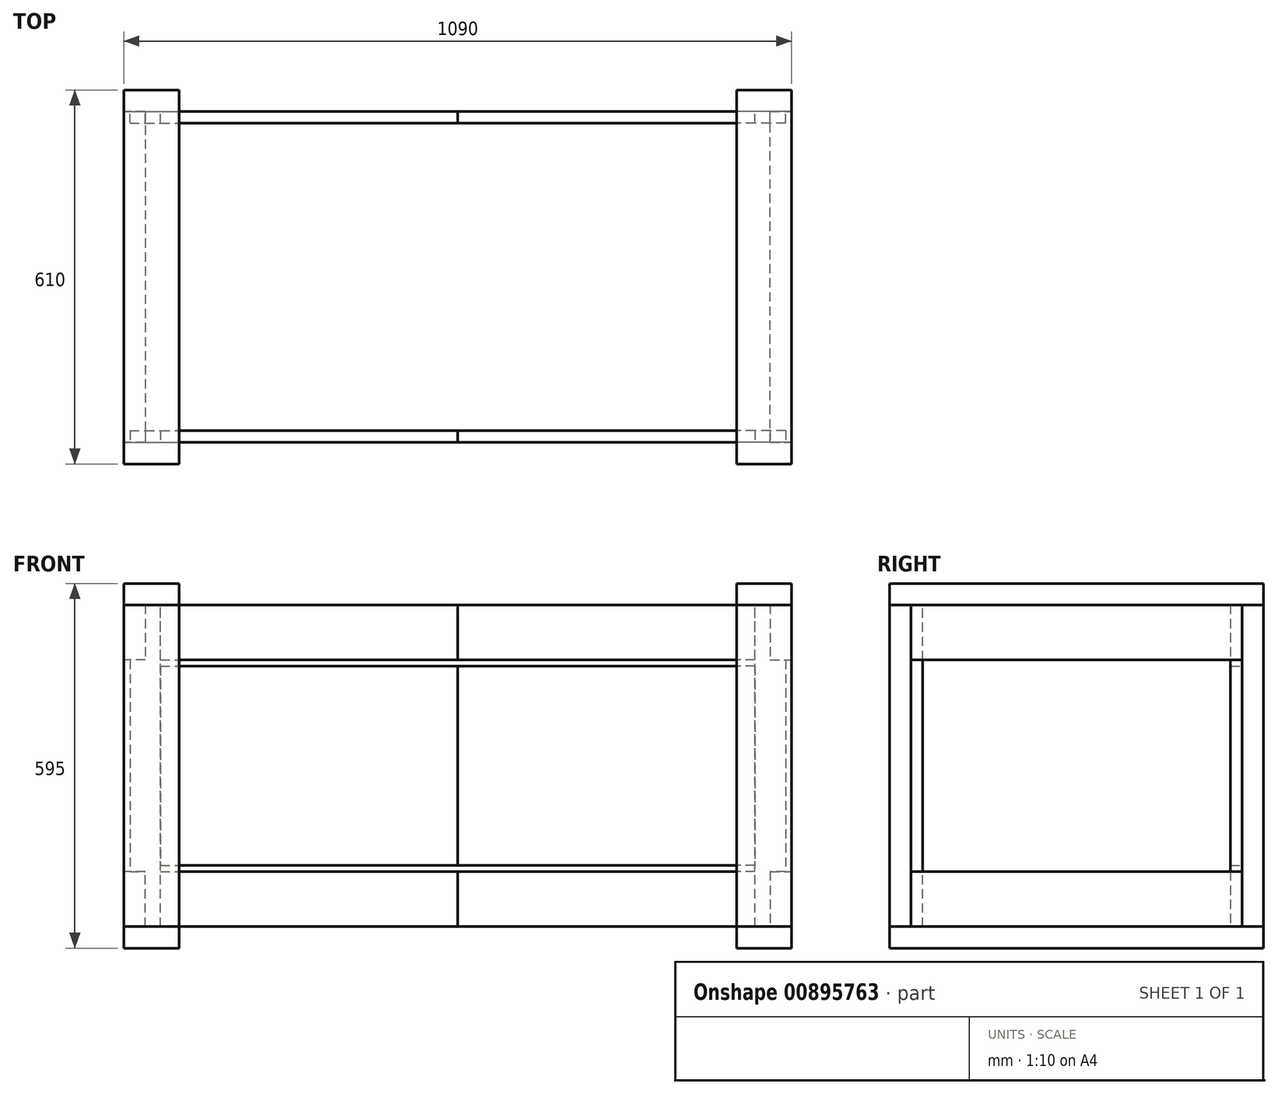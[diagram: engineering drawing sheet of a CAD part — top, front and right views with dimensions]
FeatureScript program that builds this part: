
annotation { "Feature Type Name" : "Feature", "Feature Type Description" : "" }
export const myFeature = defineFeature(function(context is Context, id is Id, definition is map)
    precondition{}
    {
        {
            var Q0;
            Q0=qCreatedBy(makeId("Top.planeOp"),FACE);
            var sketch = newSketch(context, id + "F0", { "sketchPlane" : qUnion([Q0])});
            skLineSegment(sketch, "E0.bottom", {"start": v(-545, 305) * mm, "end": v(-455, 305) * mm});
            skLineSegment(sketch, "E0.top", {"start": v(-545, -305) * mm, "end": v(-455, -305) * mm});
            skLineSegment(sketch, "E0.left", {"start": v(-545, 305) * mm, "end": v(-545, -305) * mm});
            skLineSegment(sketch, "E0.right", {"start": v(-455, 305) * mm, "end": v(-455, -305) * mm});
            skLineSegment(sketch, "E1.bottom", {"start": v(455, 305) * mm, "end": v(545, 305) * mm});
            skLineSegment(sketch, "E1.top", {"start": v(455, -305) * mm, "end": v(545, -305) * mm});
            skLineSegment(sketch, "E1.left", {"start": v(455, 305) * mm, "end": v(455, -305) * mm});
            skLineSegment(sketch, "E1.right", {"start": v(545, 305) * mm, "end": v(545, -305) * mm});
            skLineSegment(sketch, "E2", {"start": v(-455, 0) * mm, "end": v(455, 0) * mm, "construction": true});
            skSolve(sketch);
        }
        {
            var Q0;
            Q0 = qSketchRegion(id + "F0", true);
            extrude(context, id + "F1", {"entities" : qUnion([Q0]), "depth" : 35 * mm, "offsetDistance" : 25 * mm});
        }
        {
            var Q0;
            Q0=makeQuery(id+"F1.opExtrude","CAP_FACE",FACE,{"disambiguationData":[OSD([sQuery(id+"F0.wireOp",EDGE,"E0.bottom"),sQuery(id+"F0.wireOp",EDGE,"E0.top"),sQuery(id+"F0.wireOp",EDGE,"E0.left"),sQuery(id+"F0.wireOp",EDGE,"E0.right")])],"isStart":false});
            var sketch = newSketch(context, id + "F2", { "sketchPlane" : qUnion([Q0])});
            skLineSegment(sketch, "E3.bottom", {"start": v(-545, 305) * mm, "end": v(-455, 305) * mm});
            skLineSegment(sketch, "E3.top", {"start": v(-545, 270) * mm, "end": v(-455, 270) * mm});
            skLineSegment(sketch, "E3.left", {"start": v(-545, 305) * mm, "end": v(-545, 270) * mm});
            skLineSegment(sketch, "E3.right", {"start": v(-455, 305) * mm, "end": v(-455, 270) * mm});
            skLineSegment(sketch, "E4.bottom", {"start": v(-545, -305) * mm, "end": v(-455, -305) * mm});
            skLineSegment(sketch, "E4.top", {"start": v(-545, -270) * mm, "end": v(-455, -270) * mm});
            skLineSegment(sketch, "E4.left", {"start": v(-545, -305) * mm, "end": v(-545, -270) * mm});
            skLineSegment(sketch, "E4.right", {"start": v(-455, -305) * mm, "end": v(-455, -270) * mm});
            skLineSegment(sketch, "E5.bottom", {"start": v(545, 305) * mm, "end": v(455, 305) * mm});
            skLineSegment(sketch, "E5.top", {"start": v(545, 270) * mm, "end": v(455, 270) * mm});
            skLineSegment(sketch, "E5.left", {"start": v(545, 305) * mm, "end": v(545, 270) * mm});
            skLineSegment(sketch, "E5.right", {"start": v(455, 305) * mm, "end": v(455, 270) * mm});
            skLineSegment(sketch, "E6.bottom", {"start": v(545, -305) * mm, "end": v(455, -305) * mm});
            skLineSegment(sketch, "E6.top", {"start": v(545, -270) * mm, "end": v(455, -270) * mm});
            skLineSegment(sketch, "E6.left", {"start": v(545, -305) * mm, "end": v(545, -270) * mm});
            skLineSegment(sketch, "E6.right", {"start": v(455, -305) * mm, "end": v(455, -270) * mm});
            skSolve(sketch);
        }
        {
            var Q0;
            Q0 = qSketchRegion(id + "F2", true);
            extrude(context, id + "F3", {"entities" : qUnion([Q0]), "depth" : 525 * mm, "offsetDistance" : 25 * mm});
        }
        {
            var Q0;
            Q0=makeQuery(id+"F3.opExtrude","CAP_FACE",FACE,{"disambiguationData":[OSD([sQuery(id+"F2.wireOp",EDGE,"E3.bottom"),sQuery(id+"F2.wireOp",EDGE,"E3.top"),sQuery(id+"F2.wireOp",EDGE,"E3.left"),sQuery(id+"F2.wireOp",EDGE,"E3.right")])],"isStart":false});
            var sketch = newSketch(context, id + "F4", { "sketchPlane" : qUnion([Q0])});
            skLineSegment(sketch, "E7.0.0", {"start": v(-545, 305) * mm, "end": v(-545, -305) * mm});
            skLineSegment(sketch, "E7.0.1", {"start": v(-545, -305) * mm, "end": v(-455, -305) * mm});
            skLineSegment(sketch, "E7.0.2", {"start": v(-455, -305) * mm, "end": v(-455, 305) * mm});
            skLineSegment(sketch, "E7.0.3", {"start": v(-455, 305) * mm, "end": v(-545, 305) * mm});
            skLineSegment(sketch, "E7.1.0", {"start": v(455, 305) * mm, "end": v(455, -305) * mm});
            skLineSegment(sketch, "E7.1.1", {"start": v(455, -305) * mm, "end": v(545, -305) * mm});
            skLineSegment(sketch, "E7.1.2", {"start": v(545, -305) * mm, "end": v(545, 305) * mm});
            skLineSegment(sketch, "E7.1.3", {"start": v(545, 305) * mm, "end": v(455, 305) * mm});
            skSolve(sketch);
        }
        {
            var Q0;
            Q0 = qSketchRegion(id + "F4", true);
            extrude(context, id + "F5", {"entities" : qUnion([Q0]), "depth" : 35 * mm, "offsetDistance" : 25 * mm});
        }
        {
            var Q0;
            Q0=makeQuery(id+"F1.opExtrude","SWEPT_FACE",FACE,{"disambiguationData":[OSD([sQuery(id+"F0.wireOp",EDGE,"E1.right")])]});
            var sketch = newSketch(context, id + "F6", { "sketchPlane" : qUnion([Q0])});
            skLineSegment(sketch, "E8.bottom", {"start": v(-270, 35) * mm, "end": v(270, 35) * mm});
            skLineSegment(sketch, "E8.top", {"start": v(-270, 125) * mm, "end": v(270, 125) * mm});
            skLineSegment(sketch, "E8.left", {"start": v(-270, 35) * mm, "end": v(-270, 125) * mm});
            skLineSegment(sketch, "E8.right", {"start": v(270, 35) * mm, "end": v(270, 125) * mm});
            skLineSegment(sketch, "E9.bottom", {"start": v(-270, 560) * mm, "end": v(270, 560) * mm});
            skLineSegment(sketch, "E9.top", {"start": v(-270, 470) * mm, "end": v(270, 470) * mm});
            skLineSegment(sketch, "E9.left", {"start": v(-270, 560) * mm, "end": v(-270, 470) * mm});
            skLineSegment(sketch, "E9.right", {"start": v(270, 560) * mm, "end": v(270, 470) * mm});
            skSolve(sketch);
        }
        {
            var Q0;
            Q0 = qSketchRegion(id + "F6", true);
            extrude(context, id + "F7", {"entities" : qUnion([Q0]), "oppositeDirection" : true, "depth" : 35 * mm, "offsetDistance" : 25 * mm});
        }
        {
            var Q0;
            Q0=makeQuery(id+"F3.opExtrude","SWEPT_FACE",FACE,{"disambiguationData":[OSD([sQuery(id+"F2.wireOp",EDGE,"E5.top")])]});
            var sketch = newSketch(context, id + "F8", { "sketchPlane" : qUnion([Q0])});
            skLineSegment(sketch, "E10", {"start": v(485, 35) * mm, "end": v(485, 560) * mm});
            skLineSegment(sketch, "E11", {"start": v(485, 560) * mm, "end": v(510, 560) * mm});
            skLineSegment(sketch, "E12", {"start": v(510, 560) * mm, "end": v(510, 470) * mm});
            skLineSegment(sketch, "E13", {"start": v(510, 470) * mm, "end": v(535, 470) * mm});
            skLineSegment(sketch, "E14", {"start": v(535, 470) * mm, "end": v(535, 125) * mm});
            skLineSegment(sketch, "E15", {"start": v(535, 125) * mm, "end": v(510, 125) * mm});
            skLineSegment(sketch, "E16", {"start": v(510, 125) * mm, "end": v(510, 35) * mm});
            skLineSegment(sketch, "E17", {"start": v(510, 35) * mm, "end": v(485, 35) * mm});
            skSolve(sketch);
        }
        {
            var Q0;
            Q0 = qSketchRegion(id + "F8", true);
            extrude(context, id + "F9", {"entities" : qUnion([Q0]), "depth" : 19 * mm, "offsetDistance" : 25 * mm});
        }
        {
            var Q0;
            Q0=makeQuery(id+"F9.opExtrude","SWEPT_BODY",BODY,{"disambiguationData":[OSD([sQuery(id+"F8.wireOp",EDGE,"E10"),sQuery(id+"F8.wireOp",EDGE,"E11"),sQuery(id+"F8.wireOp",EDGE,"E12"),sQuery(id+"F8.wireOp",EDGE,"E13"),sQuery(id+"F8.wireOp",EDGE,"E14"),sQuery(id+"F8.wireOp",EDGE,"E15"),sQuery(id+"F8.wireOp",EDGE,"E16"),sQuery(id+"F8.wireOp",EDGE,"E17")])]});
            var Q1;
            Q1=qCreatedBy(makeId("Front.planeOp"),FACE);
            mirror(context, id + "F10", {"entities" : qUnion([Q0]), "mirrorPlane" : qUnion([Q1])});
        }
        {
            var Q0;
            Q0=makeQuery(id+"F3.opExtrude","SWEPT_FACE",FACE,{"disambiguationData":[OSD([sQuery(id+"F2.wireOp",EDGE,"E5.top")])]});
            var sketch = newSketch(context, id + "F11", { "sketchPlane" : qUnion([Q0])});
            skLineSegment(sketch, "E18.bottom", {"start": v(485, 460) * mm, "end": v(0, 460) * mm});
            skLineSegment(sketch, "E18.top", {"start": v(485, 135) * mm, "end": v(0, 135) * mm});
            skLineSegment(sketch, "E18.left", {"start": v(485, 460) * mm, "end": v(485, 135) * mm});
            skLineSegment(sketch, "E18.right", {"start": v(0, 460) * mm, "end": v(0, 135) * mm});
            skSolve(sketch);
        }
        {
            var Q0;
            Q0 = qSketchRegion(id + "F11", true);
            extrude(context, id + "F12", {"entities" : qUnion([Q0]), "depth" : 19 * mm, "offsetDistance" : 25 * mm});
        }
        {
            var Q0;
            Q0=makeQuery(id+"F3.opExtrude","SWEPT_FACE",FACE,{"disambiguationData":[OSD([sQuery(id+"F2.wireOp",EDGE,"E6.top")])]});
            var sketch = newSketch(context, id + "F13", { "sketchPlane" : qUnion([Q0])});
            skLineSegment(sketch, "E19.bottom", {"start": v(-485, 470) * mm, "end": v(0, 470) * mm});
            skLineSegment(sketch, "E19.top", {"start": v(-485, 560) * mm, "end": v(0, 560) * mm});
            skLineSegment(sketch, "E19.left", {"start": v(-485, 470) * mm, "end": v(-485, 560) * mm});
            skLineSegment(sketch, "E19.right", {"start": v(0, 470) * mm, "end": v(0, 560) * mm});
            skLineSegment(sketch, "E20.bottom", {"start": v(-485, 35) * mm, "end": v(0, 35) * mm});
            skLineSegment(sketch, "E20.top", {"start": v(-485, 125) * mm, "end": v(0, 125) * mm});
            skLineSegment(sketch, "E20.left", {"start": v(-485, 35) * mm, "end": v(-485, 125) * mm});
            skLineSegment(sketch, "E20.right", {"start": v(0, 35) * mm, "end": v(0, 125) * mm});
            skSolve(sketch);
        }
        {
            var Q0;
            Q0 = qSketchRegion(id + "F13", true);
            extrude(context, id + "F14", {"entities" : qUnion([Q0]), "depth" : 19 * mm, "offsetDistance" : 25 * mm});
        }
        {
            var Q0;
            Q0=makeQuery(id+"F7.opExtrude","SWEPT_BODY",BODY,{"disambiguationData":[OSD([sQuery(id+"F6.wireOp",EDGE,"E8.bottom"),sQuery(id+"F6.wireOp",EDGE,"E8.top"),sQuery(id+"F6.wireOp",EDGE,"E8.left"),sQuery(id+"F6.wireOp",EDGE,"E8.right")])]});
            var Q1;
            Q1=makeQuery(id+"F7.opExtrude","SWEPT_BODY",BODY,{"disambiguationData":[OSD([sQuery(id+"F6.wireOp",EDGE,"E9.bottom"),sQuery(id+"F6.wireOp",EDGE,"E9.top"),sQuery(id+"F6.wireOp",EDGE,"E9.left"),sQuery(id+"F6.wireOp",EDGE,"E9.right")])]});
            var Q2;
            Q2=makeQuery(id+"F9.opExtrude","SWEPT_BODY",BODY,{"disambiguationData":[OSD([sQuery(id+"F8.wireOp",EDGE,"E10"),sQuery(id+"F8.wireOp",EDGE,"E11"),sQuery(id+"F8.wireOp",EDGE,"E12"),sQuery(id+"F8.wireOp",EDGE,"E13"),sQuery(id+"F8.wireOp",EDGE,"E14"),sQuery(id+"F8.wireOp",EDGE,"E15"),sQuery(id+"F8.wireOp",EDGE,"E16"),sQuery(id+"F8.wireOp",EDGE,"E17")])]});
            var Q3;
            Q3=makeQuery(id+"F10.opPattern","COPY",BODY,{"derivedFrom":makeQuery(id+"F9.opExtrude","SWEPT_BODY",BODY,{"disambiguationData":[OSD([sQuery(id+"F8.wireOp",EDGE,"E10"),sQuery(id+"F8.wireOp",EDGE,"E11"),sQuery(id+"F8.wireOp",EDGE,"E12"),sQuery(id+"F8.wireOp",EDGE,"E13"),sQuery(id+"F8.wireOp",EDGE,"E14"),sQuery(id+"F8.wireOp",EDGE,"E15"),sQuery(id+"F8.wireOp",EDGE,"E16"),sQuery(id+"F8.wireOp",EDGE,"E17")])]}),"instanceName":"1"});
            var Q4;
            Q4=makeQuery(id+"F14.opExtrude","SWEPT_BODY",BODY,{"disambiguationData":[OSD([sQuery(id+"F13.wireOp",EDGE,"E19.bottom"),sQuery(id+"F13.wireOp",EDGE,"E19.top"),sQuery(id+"F13.wireOp",EDGE,"E19.left"),sQuery(id+"F13.wireOp",EDGE,"E19.right")])]});
            var Q5;
            Q5=makeQuery(id+"F14.opExtrude","SWEPT_BODY",BODY,{"disambiguationData":[OSD([sQuery(id+"F13.wireOp",EDGE,"E20.bottom"),sQuery(id+"F13.wireOp",EDGE,"E20.top"),sQuery(id+"F13.wireOp",EDGE,"E20.left"),sQuery(id+"F13.wireOp",EDGE,"E20.right")])]});
            var Q6;
            Q6=makeQuery(id+"F12.opExtrude","SWEPT_BODY",BODY,{"disambiguationData":[OSD([sQuery(id+"F11.wireOp",EDGE,"E18.bottom"),sQuery(id+"F11.wireOp",EDGE,"E18.top"),sQuery(id+"F11.wireOp",EDGE,"E18.left"),sQuery(id+"F11.wireOp",EDGE,"E18.right")])]});
            var Q7;
            Q7=qCreatedBy(makeId("Right.planeOp"),FACE);
            mirror(context, id + "F15", {"entities" : qUnion([Q0, Q1, Q2, Q3, Q4, Q5, Q6]), "mirrorPlane" : qUnion([Q7])});
        }
    });
